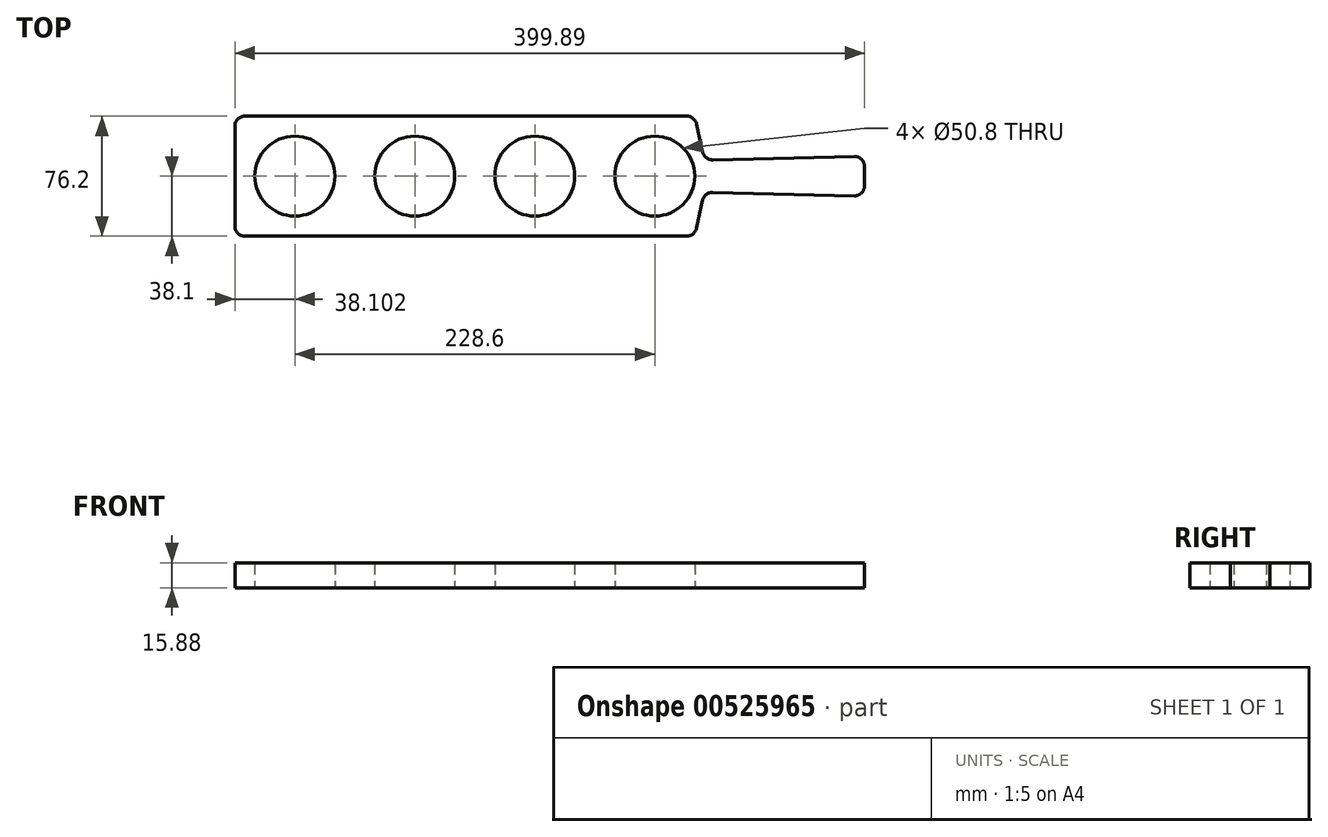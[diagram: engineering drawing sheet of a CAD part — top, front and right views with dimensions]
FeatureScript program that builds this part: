
annotation { "Feature Type Name" : "Feature", "Feature Type Description" : "" }
export const myFeature = defineFeature(function(context is Context, id is Id, definition is map)
    precondition{}
    {
        {
            var Q0;
            Q0=qCreatedBy(makeId("Top.planeOp"),FACE);
            var sketch = newSketch(context, id + "F0", { "sketchPlane" : qUnion([Q0])});
            skLineSegment(sketch, "E0", {"start": v(-133.15, 0) * mm, "end": v(-133.15, 31.75) * mm});
            skLineSegment(sketch, "E1", {"start": v(-126.8, 38.1) * mm, "end": v(153.86, 38.1) * mm});
            skLineSegment(sketch, "E2", {"start": v(160.05, 33.12) * mm, "end": v(164.01, 15.26) * mm});
            skLineSegment(sketch, "E3", {"start": v(170.37, 10.3) * mm, "end": v(260.24, 12.54) * mm});
            skLineSegment(sketch, "E4", {"start": v(266.74, 6.19) * mm, "end": v(266.74, 0) * mm});
            skArc(sketch, "E5", {"start": v(-120.45, 0) * mm, "mid": v(-95.05, 25.4) * mm, "end": v(-69.65, 0) * mm});
            skLineSegment(sketch, "E6", {"start": v(-95.05, 0) * mm, "end": v(-95.05, 25.4) * mm, "construction": true});
            skLineSegment(sketch, "E7", {"start": v(-95.05, 25.4) * mm, "end": v(-95.05, 0) * mm, "construction": true});
            skLineSegment(sketch, "E8", {"start": v(-133.15, 0) * mm, "end": v(-95.05, 0) * mm, "construction": true});
            skArc(sketch, "E9", {"start": v(-44.25, 0) * mm, "mid": v(-18.85, 25.4) * mm, "end": v(6.55, 0) * mm});
            skLineSegment(sketch, "E10", {"start": v(-18.85, 0) * mm, "end": v(-18.85, 25.4) * mm, "construction": true});
            skLineSegment(sketch, "E11", {"start": v(-95.05, 0) * mm, "end": v(-18.85, 0) * mm, "construction": true});
            skArc(sketch, "E12", {"start": v(31.95, 0) * mm, "mid": v(57.35, 25.4) * mm, "end": v(82.75, 0) * mm});
            skLineSegment(sketch, "E13", {"start": v(-18.85, 0) * mm, "end": v(57.35, 0) * mm, "construction": true});
            skLineSegment(sketch, "E14", {"start": v(57.35, 0) * mm, "end": v(57.35, 25.4) * mm, "construction": true});
            skArc(sketch, "E15", {"start": v(108.15, 0) * mm, "mid": v(133.55, 25.4) * mm, "end": v(158.95, 0) * mm});
            skLineSegment(sketch, "E16", {"start": v(57.35, 0) * mm, "end": v(133.55, 0) * mm, "construction": true});
            skLineSegment(sketch, "E17", {"start": v(133.55, 0) * mm, "end": v(133.55, 25.4) * mm, "construction": true});
            skLineSegment(sketch, "E18", {"start": v(158.95, 38.1) * mm, "end": v(158.95, 0) * mm, "construction": true});
            skLineSegment(sketch, "E19", {"start": v(165.14, 10.16) * mm, "end": v(158.95, 10.16) * mm, "construction": true});
            skLineSegment(sketch, "E20", {"start": v(165.14, 10.16) * mm, "end": v(165.14, 0) * mm, "construction": true});
            skLineSegment(sketch, "E21", {"start": v(165.14, 0) * mm, "end": v(266.74, 0) * mm, "construction": true});
            skPoint(sketch, "E22.visualSharp", {"position": v(158.95, 38.1) * mm});
            skArc(sketch, "E22.filletArc", {"start": v(160.05, 33.12) * mm, "mid": v(157.83, 36.7) * mm, "end": v(153.86, 38.1) * mm});
            skPoint(sketch, "E23.visualSharp", {"position": v(165.14, 10.16) * mm});
            skArc(sketch, "E23.filletArc", {"start": v(164.01, 15.26) * mm, "mid": v(166.3, 11.64) * mm, "end": v(170.37, 10.3) * mm});
            skPoint(sketch, "E24.visualSharp", {"position": v(266.74, 12.7) * mm});
            skArc(sketch, "E24.filletArc", {"start": v(266.74, 6.19) * mm, "mid": v(264.83, 10.74) * mm, "end": v(260.24, 12.54) * mm});
            skPoint(sketch, "E25.visualSharp", {"position": v(-133.15, 38.1) * mm});
            skArc(sketch, "E25.filletArc", {"start": v(-126.8, 38.1) * mm, "mid": v(-131.29, 36.24) * mm, "end": v(-133.15, 31.75) * mm});
            skArc(sketch, "E26.MirrorCS", {"start": v(164.01, -15.26) * mm, "mid": v(166.3, -11.64) * mm, "end": v(170.37, -10.3) * mm});
            skArc(sketch, "E27.MirrorCS", {"start": v(160.05, -33.12) * mm, "mid": v(157.83, -36.7) * mm, "end": v(153.86, -38.1) * mm});
            skLineSegment(sketch, "E28.MirrorCS", {"start": v(165.14, -10.16) * mm, "end": v(165.14, 0) * mm, "construction": true});
            skLineSegment(sketch, "E29.MirrorCS", {"start": v(266.74, -6.19) * mm, "end": v(266.74, 0) * mm});
            skArc(sketch, "E30.MirrorCS", {"start": v(-126.8, -38.1) * mm, "mid": v(-131.29, -36.24) * mm, "end": v(-133.15, -31.75) * mm});
            skArc(sketch, "E31.MirrorCS", {"start": v(266.74, -6.19) * mm, "mid": v(264.83, -10.74) * mm, "end": v(260.24, -12.54) * mm});
            skLineSegment(sketch, "E32.MirrorCS", {"start": v(-95.05, 0) * mm, "end": v(-95.05, -25.4) * mm, "construction": true});
            skLineSegment(sketch, "E33.MirrorCS", {"start": v(165.14, -10.16) * mm, "end": v(158.95, -10.16) * mm, "construction": true});
            skLineSegment(sketch, "E34.MirrorCS", {"start": v(158.95, -38.1) * mm, "end": v(158.95, 0) * mm, "construction": true});
            skPoint(sketch, "E35.MirrorP", {"position": v(158.95, -38.1) * mm});
            skLineSegment(sketch, "E36.MirrorCS", {"start": v(133.55, 0) * mm, "end": v(133.55, -25.4) * mm, "construction": true});
            skPoint(sketch, "E37.MirrorP", {"position": v(266.74, -12.7) * mm});
            skPoint(sketch, "E38.MirrorP", {"position": v(-133.15, -38.1) * mm});
            skArc(sketch, "E39.MirrorCS", {"start": v(31.95, 0) * mm, "mid": v(57.35, -25.4) * mm, "end": v(82.75, 0) * mm});
            skArc(sketch, "E40.MirrorCS", {"start": v(-44.25, 0) * mm, "mid": v(-18.85, -25.4) * mm, "end": v(6.55, 0) * mm});
            skLineSegment(sketch, "E41.MirrorCS", {"start": v(-18.85, 0) * mm, "end": v(-18.85, -25.4) * mm, "construction": true});
            skLineSegment(sketch, "E42.MirrorCS", {"start": v(-95.05, -25.4) * mm, "end": v(-95.05, 0) * mm, "construction": true});
            skArc(sketch, "E43.MirrorCS", {"start": v(-120.45, 0) * mm, "mid": v(-95.05, -25.4) * mm, "end": v(-69.65, 0) * mm});
            skLineSegment(sketch, "E44.MirrorCS", {"start": v(170.37, -10.3) * mm, "end": v(260.24, -12.54) * mm});
            skLineSegment(sketch, "E45.MirrorCS", {"start": v(160.05, -33.12) * mm, "end": v(164.01, -15.26) * mm});
            skLineSegment(sketch, "E46.MirrorCS", {"start": v(-126.8, -38.1) * mm, "end": v(153.86, -38.1) * mm});
            skLineSegment(sketch, "E47.MirrorCS", {"start": v(-133.15, 0) * mm, "end": v(-133.15, -31.75) * mm});
            skArc(sketch, "E48.MirrorCS", {"start": v(108.15, 0) * mm, "mid": v(133.55, -25.4) * mm, "end": v(158.95, 0) * mm});
            skLineSegment(sketch, "E49.MirrorCS", {"start": v(57.35, 0) * mm, "end": v(57.35, -25.4) * mm, "construction": true});
            skPoint(sketch, "E50.MirrorP", {"position": v(165.14, -10.16) * mm});
            skSolve(sketch);
        }
        {
            var Q0;
            Q0 = qSketchRegion(id + "F0", true);
            extrude(context, id + "F1", {"entities" : qUnion([Q0]), "depth" : 15.88 * mm, "offsetDistance" : 25.4 * mm});
        }
        {
            var Q0;
            Q0=makeQuery(id+"F0.imprint","IMPRINT",FACE,{"disambiguationData":[TD([[makeQuery(id+"F0.imprint","IMPRINT",EDGE,{"derivedFrom":sQuery(id+"F0.wireOp",EDGE,"E5")}),-1.0]])]});
            var Q1;
            Q1=makeQuery(id+"F0.imprint","IMPRINT",FACE,{"disambiguationData":[TD([[makeQuery(id+"F0.imprint","IMPRINT",EDGE,{"derivedFrom":sQuery(id+"F0.wireOp",EDGE,"E9")}),-1.0]])]});
            var Q2;
            Q2=makeQuery(id+"F0.imprint","IMPRINT",FACE,{"disambiguationData":[TD([[makeQuery(id+"F0.imprint","IMPRINT",EDGE,{"derivedFrom":sQuery(id+"F0.wireOp",EDGE,"E12")}),-1.0]])]});
            var Q3;
            Q3=makeQuery(id+"F0.imprint","IMPRINT",FACE,{"disambiguationData":[TD([[makeQuery(id+"F0.imprint","IMPRINT",EDGE,{"derivedFrom":sQuery(id+"F0.wireOp",EDGE,"E15")}),-1.0]])]});
            extrude(context, id + "F2", {"entities" : qUnion([Q0, Q1, Q2, Q3]), "operationType" : NewBodyOperationType.ADD, "depth" : 7.94 * mm, "offsetDistance" : 25.4 * mm});
        }
    });
